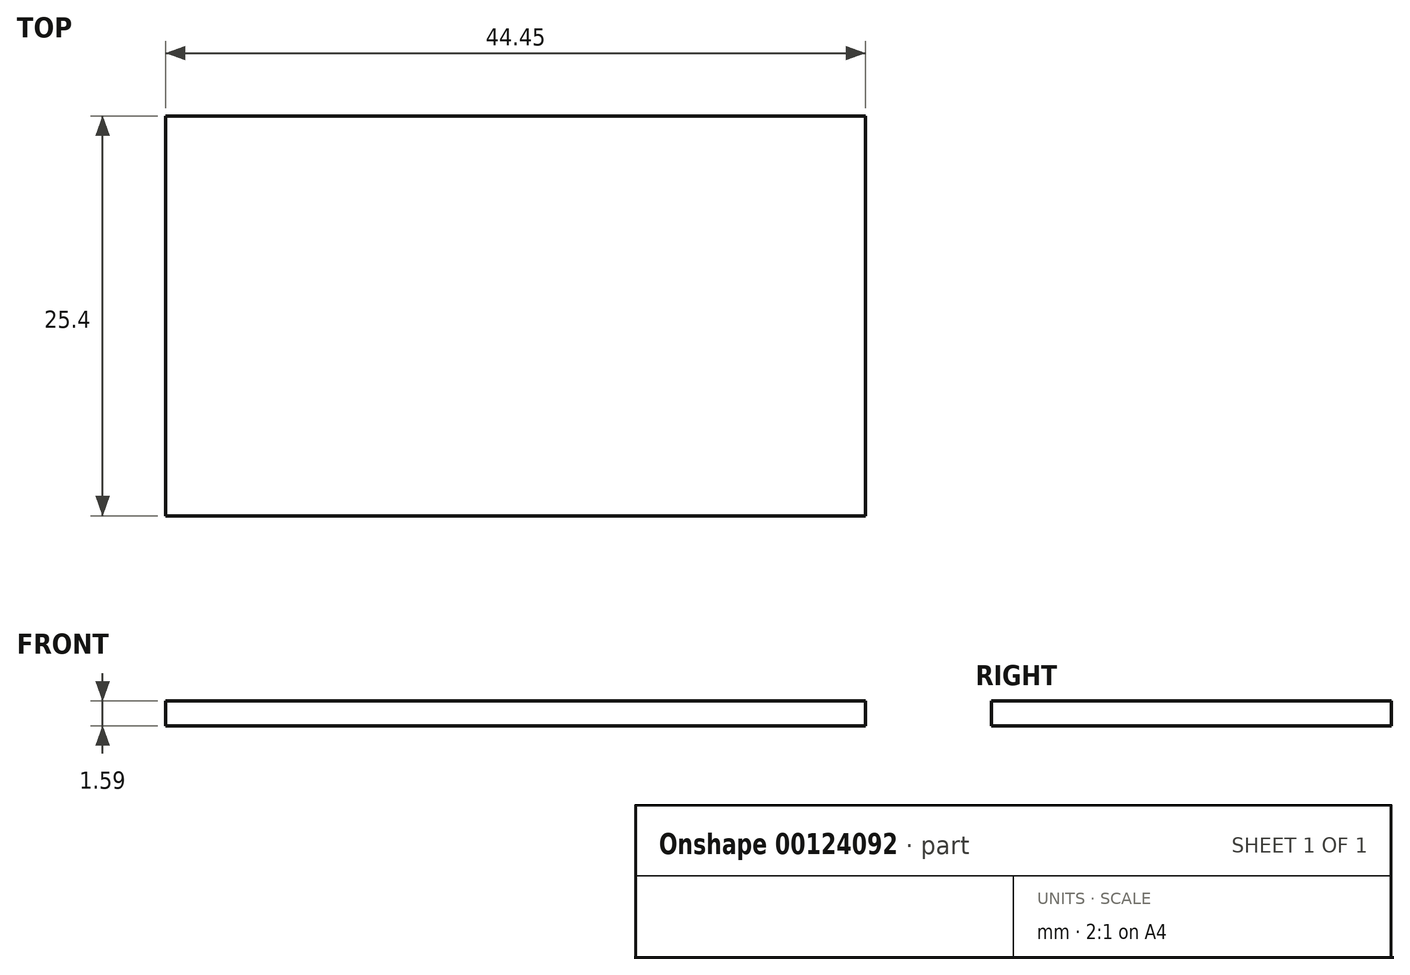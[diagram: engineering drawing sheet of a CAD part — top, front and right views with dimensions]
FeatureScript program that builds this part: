
annotation { "Feature Type Name" : "Feature", "Feature Type Description" : "" }
export const myFeature = defineFeature(function(context is Context, id is Id, definition is map)
    precondition{}
    {
        {
            var Q0;
            Q0=qCreatedBy(makeId("Top.planeOp"),FACE);
            var sketch = newSketch(context, id + "F0", { "sketchPlane" : qUnion([Q0])});
            skLineSegment(sketch, "E0.bottom", {"start": v(-22.77, 16.18) * mm, "end": v(21.68, 16.18) * mm});
            skLineSegment(sketch, "E0.top", {"start": v(-22.77, -9.22) * mm, "end": v(21.68, -9.22) * mm});
            skLineSegment(sketch, "E0.left", {"start": v(-22.77, 16.18) * mm, "end": v(-22.77, -9.22) * mm});
            skLineSegment(sketch, "E0.right", {"start": v(21.68, 16.18) * mm, "end": v(21.68, -9.22) * mm});
            skSolve(sketch);
        }
        {
            var Q0;
            Q0 = qSketchRegion(id + "F0", true);
            extrude(context, id + "F1", {"entities" : qUnion([Q0]), "depth" : 1.59 * mm});
        }
    });
